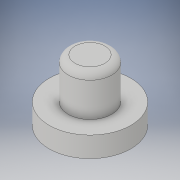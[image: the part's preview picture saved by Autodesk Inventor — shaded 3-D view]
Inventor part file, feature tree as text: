
AUTODESK INVENTOR PART (.ipt)
format: ipt  version: 2019 (Build 230136000, 136)  size: 116,224 bytes
history: native  units: mm
features: extrude x2, sketch x2, other x1, fillet x1
ambient origin geometry x8: Origin, YZ Plane, XZ Plane, XY Plane, X Axis, Y Axis, Z Axis, Center Point
bodies: Body1 (feature_tree)
feature tree (6):
  other  "Твердое тело1"
  extrude  "Выдавливание1"  Depth=6.0mm
  extrude  "Выдавливание2"  Depth=1.5mm TaperAngle=0.0deg
  fillet  "Сопряжение1"  Radius=3.2mm
  sketch  "Эскиз1"
  sketch  "Эскиз2"
